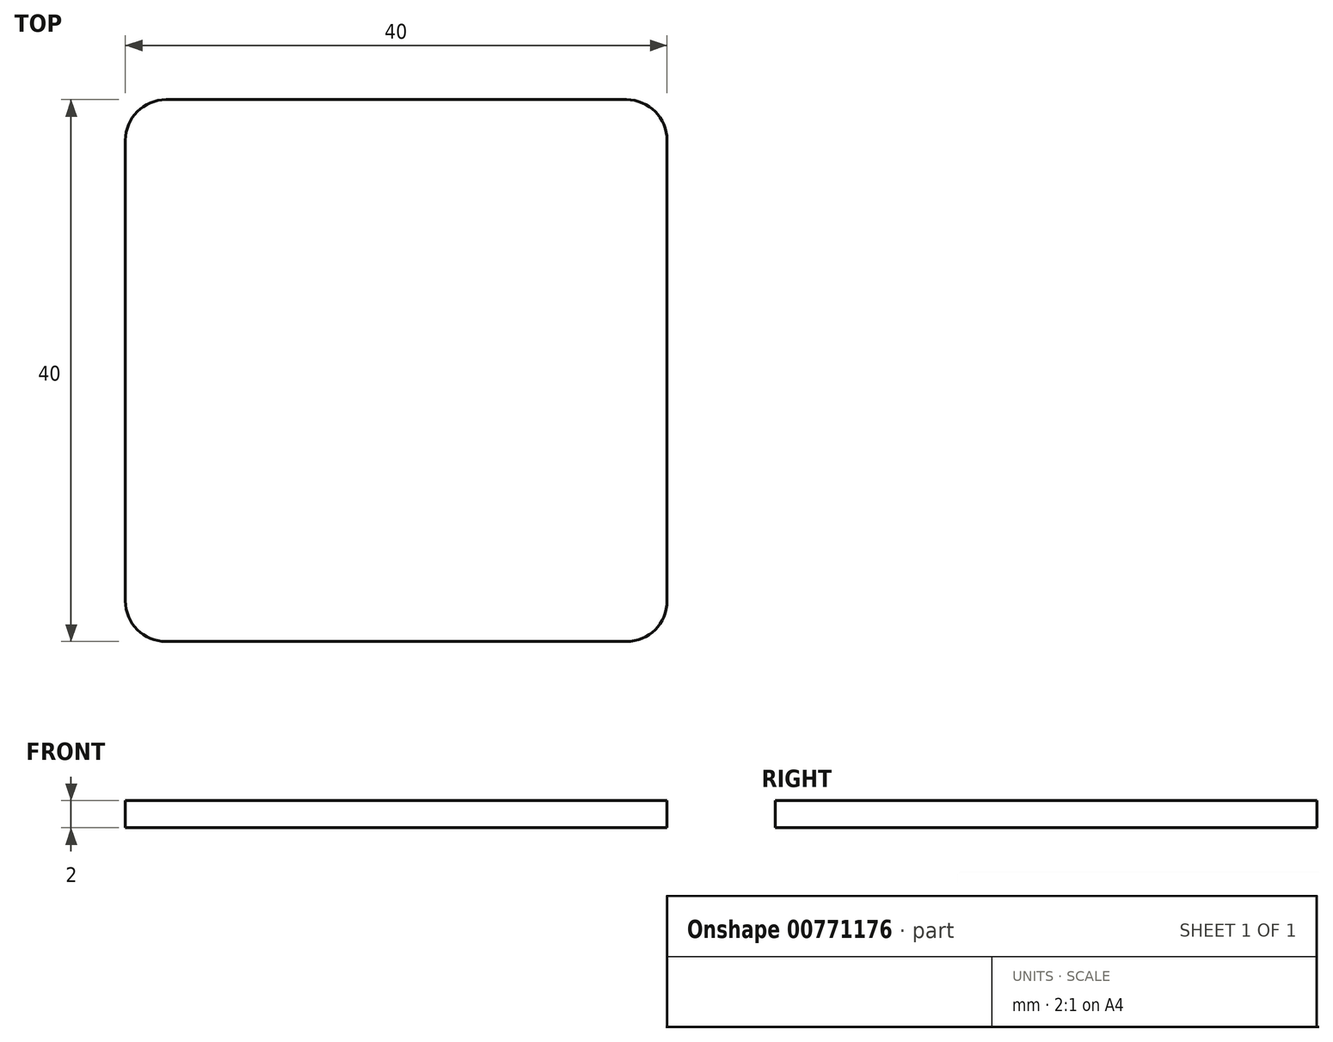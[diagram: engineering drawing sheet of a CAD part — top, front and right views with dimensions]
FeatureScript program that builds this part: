
annotation { "Feature Type Name" : "Feature", "Feature Type Description" : "" }
export const myFeature = defineFeature(function(context is Context, id is Id, definition is map)
    precondition{}
    {
        {
            var Q0;
            Q0=qCreatedBy(makeId("Top.planeOp"),FACE);
            var sketch = newSketch(context, id + "F0", { "sketchPlane" : qUnion([Q0])});
            skLineSegment(sketch, "E0.bottom", {"start": v(0, 0) * mm, "end": v(-40, 0) * mm});
            skLineSegment(sketch, "E0.top", {"start": v(0, 40) * mm, "end": v(-40, 40) * mm});
            skLineSegment(sketch, "E0.left", {"start": v(0, 0) * mm, "end": v(0, 40) * mm});
            skLineSegment(sketch, "E0.right", {"start": v(-40, 0) * mm, "end": v(-40, 40) * mm});
            skSolve(sketch);
        }
        {
            var Q0;
            Q0 = qSketchRegion(id + "F0", true);
            extrude(context, id + "F1", {"entities" : qUnion([Q0]), "depth" : 2 * mm, "offsetDistance" : 25 * mm});
        }
        {
            var Q0;
            Q0=makeQuery(id+"F1.opExtrude","SWEPT_EDGE",EDGE,{"disambiguationData":[OSD([sQuery(id+"F0.wireOp",EDGE,"E0.top"),sQuery(id+"F0.wireOp",EDGE,"E0.right")])]});
            var Q1;
            Q1=makeQuery(id+"F1.opExtrude","SWEPT_EDGE",EDGE,{"disambiguationData":[OSD([sQuery(id+"F0.wireOp",EDGE,"E0.top"),sQuery(id+"F0.wireOp",EDGE,"E0.left")])]});
            var Q2;
            Q2=makeQuery(id+"F1.opExtrude","SWEPT_EDGE",EDGE,{"disambiguationData":[OSD([sQuery(id+"F0.wireOp",EDGE,"E0.bottom"),sQuery(id+"F0.wireOp",EDGE,"E0.left")])]});
            var Q3;
            Q3=makeQuery(id+"F1.opExtrude","SWEPT_EDGE",EDGE,{"disambiguationData":[OSD([sQuery(id+"F0.wireOp",EDGE,"E0.bottom"),sQuery(id+"F0.wireOp",EDGE,"E0.right")])]});
            fillet(context, id + "F2", {"entities" : qUnion([Q0, Q1, Q2, Q3]), "radius" : 3 * mm, "tangentPropagation" : true, "allowEdgeOverflow" : false});
        }
    });
